# Revit family: ENG Małkowski Martech_Brama_Marc-KDS
name_source: partatom
category: Mechanical Equipment
units: mm (PartAtom-declared; Revit-internal decimal feet)

## family parameters
Always vertical = No
Classification = None
Cut with Voids When Loaded = No
OmniClass Number = 23.30.10.00
OmniClass Title = Doors
Part Type = Normal
Room Calculation Point = Yes
Round Connector Dimension = Use Diameter
Shared = No
Work Plane-Based = Yes

## types (1)
- Shaft box ceiling-suspended
    Construction type = Static smoke barriers
    Curtain sheet = non-flammable fiberglass fabric, standard gray-silver color, with a load strip attached to the bottom edge of the coat
    Fire rating = D, DH
    Height = 0 mm  [stored 0 ft]
    IfcExportAs = IfcDoor
    Installation elements = steel angle bar 50x50x6 and flat bar 40x3 made of steel sheet, fixing with M6x25 hexagonal bolts and M10 steel anchors
    Manufacturer = Małkowski - Martech S.A.
    Model = Marc - KDS
    Type Image = 062-700x600-px-scale-730-547.jpg
    URL = https://www.malkowski.pl
    Wall Closure = By host
    Width = 0 mm  [stored 0 ft]

note: [stored X ft] marks values corroborated as IEEE doubles in the binary element streams (Revit-internal decimal feet)
